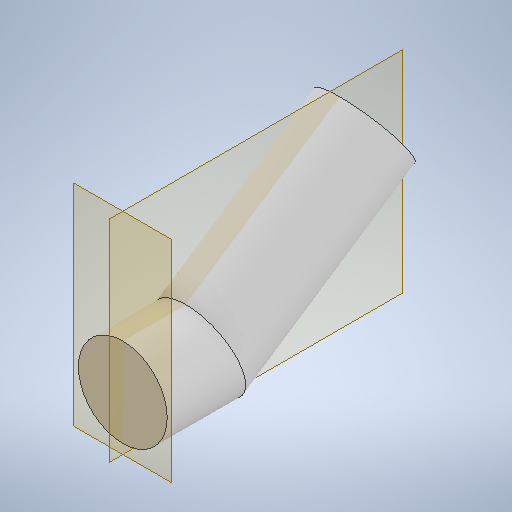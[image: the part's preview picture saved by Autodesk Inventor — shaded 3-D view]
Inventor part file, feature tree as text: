
AUTODESK INVENTOR PART (.ipt)
format: ipt  version: 2025.2 (Build 292293000, 293)  size: 241,152 bytes
history: native  units: mm
features: sketch x2, other x1, sweep x1
ambient origin geometry x8: Origin, YZ Plane, XZ Plane, XY Plane, X Axis, Y Axis, Z Axis, Center Point
bodies: Body1 (feature_tree)
feature tree (4):
  other  "Sólido1"
  sweep  "Varredura1"
  sketch  "Esboço1"  dims[d0=0.0mm d1=0.0mm]
  sketch  "Esboço2"
